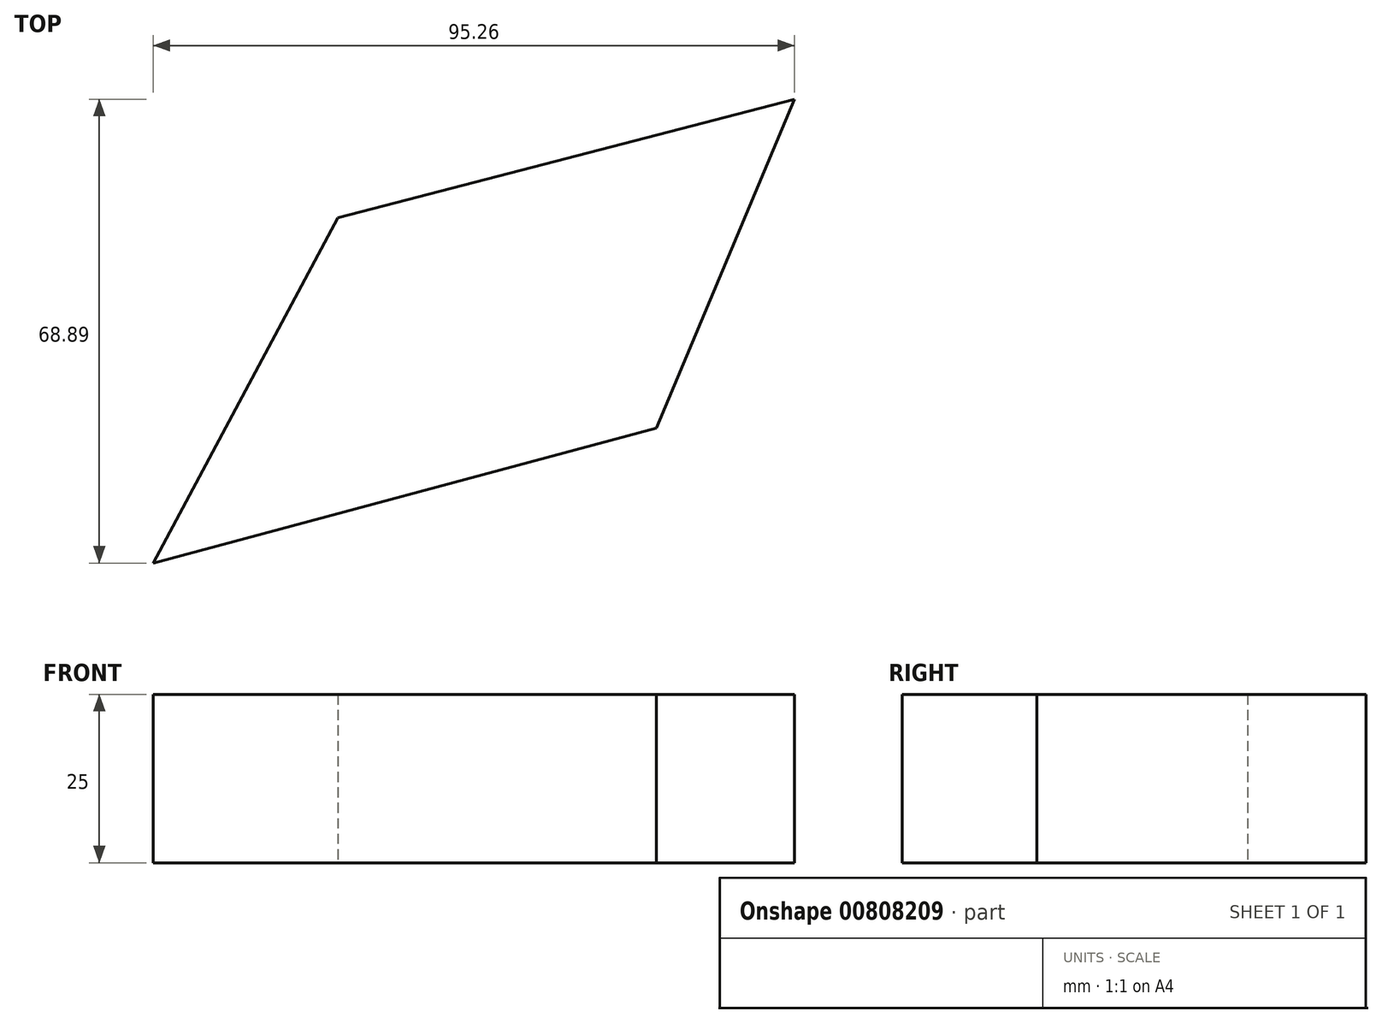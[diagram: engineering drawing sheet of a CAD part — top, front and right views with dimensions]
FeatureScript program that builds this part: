
annotation { "Feature Type Name" : "Feature", "Feature Type Description" : "" }
export const myFeature = defineFeature(function(context is Context, id is Id, definition is map)
    precondition{}
    {
        {
            var Q0;
            Q0=qCreatedBy(makeId("Top.planeOp"),FACE);
            var sketch = newSketch(context, id + "F0", { "sketchPlane" : qUnion([Q0])});
            skLineSegment(sketch, "E0", {"start": v(-20.5, -48.86) * mm, "end": v(0, 0) * mm});
            skLineSegment(sketch, "E1", {"start": v(0, 0) * mm, "end": v(-67.78, -17.6) * mm});
            skLineSegment(sketch, "E2", {"start": v(-67.78, -17.6) * mm, "end": v(-95.26, -68.9) * mm});
            skLineSegment(sketch, "E3", {"start": v(-95.26, -68.9) * mm, "end": v(-20.5, -48.86) * mm});
            skSolve(sketch);
        }
        {
            var Q0;
            Q0 = qSketchRegion(id + "F0", true);
            extrude(context, id + "F1", {"entities" : qUnion([Q0]), "depth" : 25 * mm, "offsetDistance" : 25 * mm});
        }
    });
